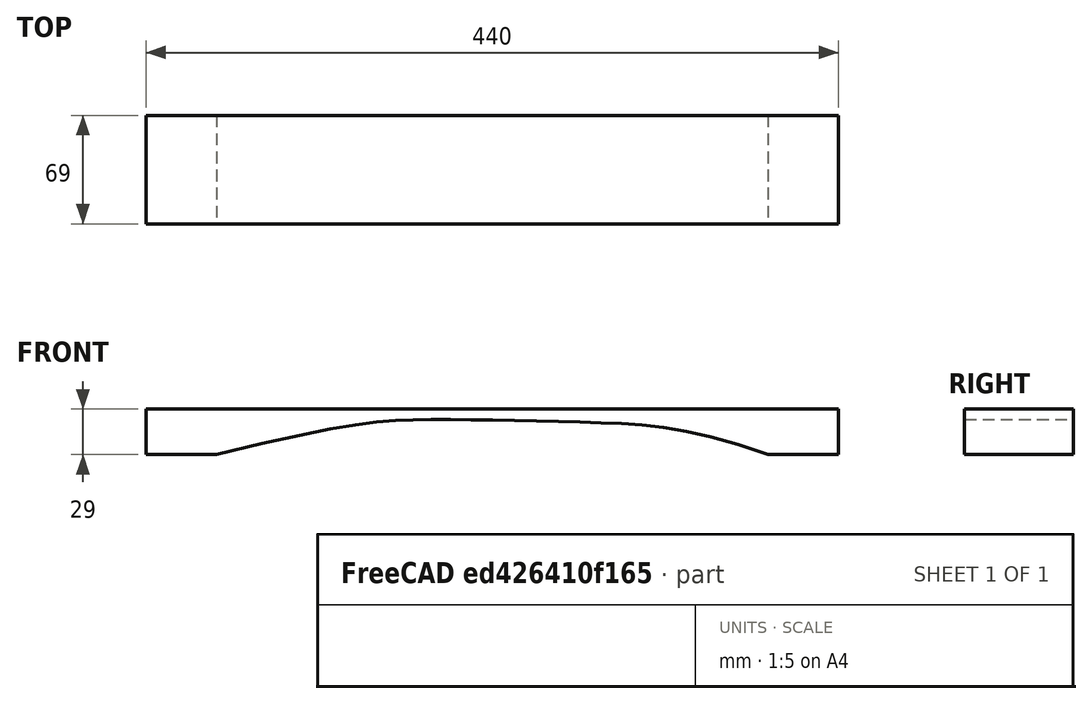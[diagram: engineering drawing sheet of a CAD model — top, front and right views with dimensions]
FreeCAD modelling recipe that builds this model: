
FCSTD DOCUMENT  (FreeCAD 0.20R29410 (Git))
Label: EuropeanOak-6.67-Bar
License: All rights reserved
LicenseURL: http://en.wikipedia.org/wiki/All_rights_reserved
objects: Fem::FemResultObjectPython×3, Fem::FemPostDataAtPointFilter×3, Fem::FemPostWarpVectorFilter×3, Fem::FemPostPipeline×3, Sketcher::SketchObject×1, Part::Extrusion×1, Fem::FemSolverObjectPython×1, App::MaterialObjectPython×1, Fem::ConstraintDisplacement×1, Fem::FemMeshShapeNetgenObject×1, Fem::FemMeshObjectPython×1, App::TextDocument×1, Fem::FemAnalysis×1
note: 2 computed .brp shape members not serialized (recipe doc carries the construction recipe); baked Part::Feature solids carry a one-line shape summary decoded from their .brp

FEATURE [Sketcher::SketchObject] Sketch
  FullyConstrained = true
  Placement = pos=(0,0,0) rot=(1,0,0;1.5708rad)
  sketch-geometry (12):
    g0: LineSegment StartX=44.78 StartY=0 StartZ=0 EndX=0 EndY=0 EndZ=0
    g1: LineSegment StartX=0 StartY=0 StartZ=0 EndX=0 EndY=29 EndZ=0
    g2: LineSegment StartX=0 StartY=29 StartZ=0 EndX=440 EndY=29 EndZ=0
    g3: LineSegment StartX=440 StartY=29 StartZ=0 EndX=440 EndY=0 EndZ=0
    g4: LineSegment StartX=440 StartY=0 StartZ=0 EndX=395.22 EndY=0 EndZ=0
    g5-g10: Circle x6 (B-spline internal-alignment scaffolding for g11; pole/knot coordinates omitted)
    g11: BSplineCurve PolesCount=6 KnotsCount=4 Degree=3 IsPeriodic=0
  constraints (38):
    c: DistanceX(g0) = 0
    c: DistanceY(g0) = 0
    c: Distance(g1,g1) = 29
    c: Distance(g2,g2) = 440
    c: DistanceX(g0,g0) = 44.78
    c: DistanceX(g4,g4) = 44.78
    c: Horizontal(g0)
    c: Vertical(g1)
    c: Horizontal(g2)
    c: Vertical(g3)
    c: Horizontal(g4)
    c: Equal(g3,g1)
    c: Coincident(g0,g1)
    c: Coincident(g1,g2)
    c: Coincident(g2,g3)
    c: Coincident(g3,g4)
    c: DistanceX(g6) = 343.71
    c: DistanceY(g6) = 18.63
    c: DistanceX(g7) = 284.82
    c: DistanceY(g7) = 20.42
    c: DistanceX(g8) = 168.2
    c: DistanceY(g8) = 23.47
    c: DistanceX(g9) = 126.8
    c: DistanceY(g9) = 20.13
    c: Weight(g5) = 1
    c: InternalAlignment(g5,g11)
    c: Weight(g6) = 1
    c: InternalAlignment(g6,g11)
    c: Weight(g7) = 1
    c: InternalAlignment(g7,g11)
    c: Weight(g8) = 1
    c: InternalAlignment(g8,g11)
    c: Weight(g9) = 1
    c: InternalAlignment(g9,g11)
    c: Weight(g10) = 1
    c: InternalAlignment(g10,g11)
    c: Coincident(g4,g11)
    c: Coincident(g0,g11)
FEATURE [Part::Extrusion] Bar
  Base = -> Sketch
  Dir = (0,-1,2e-16)
  DirMode = 2
  FaceMakerClass = Part::FaceMakerBullseye
  LengthFwd = 69
  LengthRev = 0
  Solid = true
  Symmetric = false
FEATURE [Fem::FemSolverObjectPython] SolverCcxTools  # FEM object (typed FeaturePython)
  AnalysisType = 1
  BeamShellResultOutput3D = false
  BucklingFactors = 1
  EigenmodeHighLimit = 20000
  EigenmodeLowLimit = 100
  EigenmodesCount = 6
  GeometricalNonlinearity = 0
  IterationsControlParameterCutb = 0.25,0.5,0.75,0.85,,,1.5,
  IterationsControlParameterIter = 4,8,9,200,10,400,,200,,
  IterationsControlParameterTimeUse = false
  IterationsThermoMechMaximum = 2000
  IterationsUserDefinedIncrementations = false
  IterationsUserDefinedTimeStepLength = false
  MaterialNonlinearity = 0
  MatrixSolverType = 0
  SplitInputWriter = false
  ThermoMechSteadyState = false
  TimeEnd = 1
  TimeInitialStep = 0.01
FEATURE [App::MaterialObjectPython] MaterialSolid  # material (typed FeaturePython)
  Category = 0
  Material = CompressiveStrength=7800 kPa,Density=670 kg/m^3,Name=White European Oak,PoissonRatio=0.37,ShearModulus=11.6 MPa,UltimateTensileStrength=97.1 MPa,+1 more (map truncated)
FEATURE [Fem::ConstraintDisplacement] FemConstraintDisplacement
  NormalDirection = (0,-2e-16,-1)
  Normals = (116) [(0,-2.2e-16,-1),(0,-2.2e-16,-1),(0,-2.2e-16,-1),(0,-2.2e-16,-1),(0,-2.2e-16,-1),(0,-2.2e-16,-1),(0,-2.2e-16,-1),(0,-2.2e-16,-1),(0,-2.2e-16,-1),+107 more]
  Points = (116) [(44.78,-69,1.518e-14),(29.8533,-69,1.518e-14),(14.9267,-69,1.518e-14),(0,-69,1.518e-14),(44.78,-46,1.012e-14),(29.8533,-46,1.012e-14),+110 more]
  References = -> [Bar]
  rotxFix = false
  rotxFree = true
  rotyFix = false
  rotyFree = true
  rotzFix = false
  rotzFree = true
  xDisplacement = 0
  xFix = false
  xFree = true
  xRotation = 0
  yDisplacement = 0
  yFix = true
  yFree = false
  yRotation = 0
  zDisplacement = 0
  zFix = false
  zFree = true
  zRotation = 0
FEATURE [Fem::FemMeshShapeNetgenObject] FEMMeshNetgen
  Fineness = 4
  GrowthRate = 0.3
  MaxSize = 10
  NbSegsPerEdge = 1
  NbSegsPerRadius = 2
  Optimize = true
  SecondOrder = true
  Shape = -> Bar
FEATURE [Fem::FemMeshObjectPython] ResultMesh  # FEM object (typed FeaturePython)
FEATURE [Fem::FemResultObjectPython] CCX_EigenMode_4_Results  # FEM object (typed FeaturePython)
  DisplacementLengths = [39.76,39.7598,79.6677,79.6678,75.5133,75.5134,78.2101,78.2101,82.2686,82.2687,40.3463,40.3463,49.9702,60.3738,71.2113,79.6902,78.2819,67.6655,57.1744,46.6504,36.1976,25.8005,15.5235,6.29701,7.66099,17.2706,27.454,37.6931,47.9022,57.8919,+6003 more]
  DisplacementVectors = (6033) [(-25.6275,0,-30.3988),(-25.6276,0,-30.3985),(-25.6346,0,-75.4308),(-25.6347,0,-75.4309),(3.52913,0,-75.4308),(3.52922,0,-75.4309),+6027 more]
  Eigenmode = 4
  EigenmodeFrequency = 130.981
  MaxShear = [1.94221,1.98751,0.103232,0.0983929,0.0331848,0.0304907,0.0614545,0.0502109,0.0808435,0.106342,2.57597,2.6428,1.8565,0.930537,0.220849,0.0864277,0.0953536,0.131411,0.619313,1.415,2.5679,4.35116,6.86131,10.7409,16.0052,23.8974,34.7322,+6006 more]
  Mesh = -> ResultMesh
  NodeNumbers = [1,2,3,4,5,6,7,8,9,10,11,12,13,14,15,16,17,18,19,20,21,22,23,24,25,26,27,28,29,30,31,32,33,34,35,36,37,38,39,40,41,42,43,44,45,46,47,48,49,50,51,52,53,54,55,56,57,58,59,60,61,62,63,64,65,66,67,68,69,+5964 more]
  NodeStrainXX = [-0.000295432,-0.00030086,2.45907e-06,6.97468e-07,-5.1885e-07,-3.24382e-07,-4.21691e-06,-9.08742e-07,4.74133e-06,9.43238e-08,-0.000403341,-0.000414238,-0.000302757,-0.000149992,-3.57943e-05,-8.17154e-06,6.68297e-06,2.06383e-05,0.000100366,+6014 more]
  NodeStrainXY = [1.45659e-07,-1.30851e-06,7.3266e-08,-3.18589e-07,1.00641e-06,-1.16253e-06,-1.18173e-07,1.44421e-06,3.08405e-07,-2.86151e-07,-4.66795e-06,6.44721e-07,2.1901e-07,9.09316e-07,-9.04872e-07,-8.87817e-07,5.29394e-07,6.16621e-07,4.68293e-07,+6014 more]
  NodeStrainXZ = [9.55077e-05,9.82858e-05,1.3336e-05,1.26362e-05,4.07302e-06,3.65005e-06,-7.61538e-06,-6.238e-06,-1.00674e-05,-1.36201e-05,-8.9149e-05,-8.78961e-05,9.79878e-06,1.08867e-05,2.8033e-06,4.45075e-06,8.31595e-06,3.36125e-06,3.86984e-06,+6014 more]
  NodeStrainYY = [-2.86839e-11,-2.76119e-11,-2.19101e-07,-2.12745e-07,0,0,9.10746e-13,0,4.5424e-14,-1.13863e-07,1.03284e-06,-4.94041e-07,-2.90461e-07,-2.61899e-08,3.27789e-13,5.90685e-07,-1.07211e-07,-5.50318e-12,-6.07976e-13,1.50491e-12,1.64431e-12,+6012 more]
  NodeStrainYZ = [-1.68788e-06,6.43692e-07,1.89881e-07,-8.10458e-07,6.91778e-07,-7.41743e-07,1.089e-07,-7.08997e-07,3.35057e-07,-1.96548e-07,-2.12959e-06,-7.26048e-07,7.29178e-07,9.46325e-08,4.64683e-07,3.25619e-07,-3.56037e-07,2.91515e-07,6.07891e-07,+6014 more]
  NodeStrainZZ = [0.000168837,0.000173793,1.74266e-06,3.03079e-06,-1.15479e-06,-1.08002e-06,2.81428e-07,-1.77176e-06,-7.60119e-07,3.70239e-06,0.000238139,0.000245892,0.000176727,8.95502e-05,2.09848e-05,1.222e-05,-1.14644e-05,-1.26343e-05,-5.95246e-05,+6014 more]
  NodeStressXX = [-3.67972,-3.72691,0.0628778,0.0441046,-0.0224424,-0.0179732,-0.0759594,-0.0365453,0.0805206,0.0412805,-4.92836,-5.06409,-3.73338,-1.82631,-0.440011,-0.0121447,-0.00211965,0.247812,1.22625,2.81066,5.10876,8.66193,13.6774,21.4132,31.8491,+6008 more]
  NodeStressXY = [0.001127,-0.0101242,0.000566876,-0.002465,0.00778681,-0.00899475,-0.00091433,0.0111742,0.0023862,-0.00221402,-0.036117,0.00498836,0.00169453,0.00703558,-0.0070012,-0.00686924,0.00409604,0.00477093,0.00362329,0.00546462,0.00611664,0.0117295,+6011 more]
  NodeStressXZ = [0.738965,0.760459,0.103184,0.0977689,0.0315139,0.0282412,-0.0589219,-0.0482648,-0.0778938,-0.105382,-0.689766,-0.680072,0.0758154,0.0842329,0.0216898,0.0344365,0.0643424,0.0260067,0.0299418,0.0372396,0.0480075,0.144833,0.188619,0.359045,+6009 more]
  NodeStressYY = [-1.3939,-1.39909,0.0421562,0.0370621,-0.0184279,-0.0154634,-0.0433322,-0.0295141,0.0438358,0.0396697,-1.79962,-1.86286,-1.39313,-0.665992,-0.163062,0.0556506,-0.0546569,0.0881289,0.449692,1.03316,1.88059,3.1918,5.04584,7.90212,11.7296,+6008 more]
  NodeStressYZ = [-0.0130595,0.00498039,0.00146915,-0.0062707,0.00535244,-0.00573903,0.000842587,-0.00548567,0.00259241,-0.00152073,-0.0164771,-0.0056176,0.00564181,0.000732193,0.00359536,0.00251939,-0.00275474,0.00225552,0.00470339,0.000629211,0.0102274,+6012 more]
  NodeStressZZ = [-0.0875655,-0.0544186,0.0573349,0.0621581,-0.0273628,-0.0238198,-0.0411548,-0.0432226,0.0379546,0.0691969,0.0349169,0.0434882,-0.0235053,0.0270803,-0.000698001,0.145629,-0.14253,-0.00962542,-0.0108639,-0.0183342,-0.0260827,-0.0354289,+6011 more]
  PrincipalMax = [0.0586206,0.0968262,0.163344,0.151662,0.00980705,0.0115957,0.00291323,0.0119308,0.139988,0.161542,0.129061,0.132508,-0.0219331,0.0309022,0.000434787,0.152829,0.0230074,0.250565,1.22699,2.81117,5.10922,8.66437,13.68,21.4192,31.8554,47.6937,+6007 more]
  PrincipalMed = [-1.394,-1.39905,0.0421444,0.0367868,-0.0214776,-0.0194664,-0.0433638,-0.0327217,0.0440225,0.0397472,-1.79924,-1.86287,-1.39315,-0.665952,-0.162942,0.0563315,-0.054614,0.0880079,0.44972,1.03314,1.88063,3.19189,5.04582,7.90242,11.7308,17.607,+6007 more]
  PrincipalMin = [-3.8258,-3.8782,-0.0431199,-0.0451239,-0.0565626,-0.0493857,-0.119996,-0.0884911,-0.0216993,-0.051142,-5.02288,-5.1531,-3.73493,-1.83017,-0.441264,-0.020026,-0.1677,-0.0122576,-0.0116343,-0.0188246,-0.0265857,-0.0379518,-0.0426047,+6010 more]
  ResultType = Fem::ResultMechanical
  Stats = [-25.6347,25.9336,-0.0014929,0.00150639,-78.0742,106.569,0.763143,106.571,0.00875485,578.029,-17.7689,656.814,-245.14,243.457,-660.917,13.3385,0.00500687,330.025,0,0,0,0,0,0,0,0]
  Time = 0
  vonMises = [3.39945,3.4774,0.179704,0.171217,0.0575092,0.0528146,0.107519,0.0871454,0.140839,0.184837,4.50848,4.62302,3.25196,1.62859,0.386816,0.150035,0.166107,0.229732,1.08425,2.47759,4.49654,7.61939,12.0156,18.8097,28.0262,41.8517,60.8254,89.0578,+6005 more]
FEATURE [Fem::FemResultObjectPython] CCX_EigenMode_5_Results  # FEM object (typed FeaturePython)
  DisplacementLengths = [26.3796,26.3798,75.2426,75.2436,72.5186,72.5197,66.9934,66.9937,69.7371,69.7373,24.8668,24.8666,32.4211,43.6382,56.3709,66.5666,65.5722,54.3498,41.963,29.9872,19.4006,13.6524,18.0852,28.1095,39.5246,51.2307,62.6848,73.5978,83.6074,92.0931,+6003 more]
  DisplacementVectors = (6033) [(-25.4039,0,-7.10821),(-25.4048,0,-7.10547),(-25.5047,0,-70.7881),(-25.5057,0,-70.7888),(15.7479,0,-70.7881),(15.7491,0,-70.7889),(13.7643,0,65.5642),+6026 more]
  Eigenmode = 5
  EigenmodeFrequency = 524.853
  MaxShear = [26.7626,27.199,1.48512,1.42254,0.486505,0.449464,0.798575,0.653579,1.03961,1.37504,31.7685,32.4682,23.5642,12.2071,3.07377,1.14814,1.25091,2.14019,8.84753,19.0198,32.825,52.8687,79.4878,117.768,166.133,232.711,316.08,427.182,565.021,+6004 more]
  Mesh = -> ResultMesh
  NodeNumbers = <same value as first occurrence — deduplicated (x3 in doc)>
  NodeStrainXX = [-0.00408177,-0.00412737,3.00783e-05,3.41267e-06,-5.40461e-06,-2.55257e-06,5.30576e-05,9.77597e-06,-5.71406e-05,4.7807e-06,0.00498277,0.00509671,0.00384536,0.00197003,0.000497902,0.000108019,-8.39451e-05,-0.000338979,-0.00143456,-0.00308963,+6013 more]
  NodeStrainXY = [2.79895e-06,-2.10261e-05,1.39684e-06,-4.19528e-06,1.50869e-05,-1.72684e-05,1.41845e-06,-1.90974e-05,-3.66192e-06,3.22767e-06,5.51717e-05,-6.08049e-06,-1.80597e-06,-1.16568e-05,1.16464e-05,1.14972e-05,-7.12222e-06,-7.95565e-06,-5.67877e-06,+6014 more]
  NodeStrainXZ = [0.00129631,0.00132659,0.00019192,0.000182059,5.9471e-05,5.36167e-05,9.95335e-05,8.10169e-05,0.000130455,0.000175322,0.0010785,0.00106303,-0.00011805,-0.000139037,-4.14354e-05,-6.15708e-05,-0.000112463,-4.93491e-05,-5.44258e-05,-6.54727e-05,+6013 more]
  NodeStrainYY = [-3.65881e-10,-3.2824e-10,-2.99822e-06,-3.00817e-06,0,0,-1.29471e-11,0,1.27525e-13,1.60707e-06,-1.21685e-05,6.27541e-06,2.93115e-06,6.31625e-07,-4.22181e-12,-7.76339e-06,1.4982e-06,6.78318e-11,2.77572e-12,-2.31363e-11,-3.02419e-11,+6012 more]
  NodeStrainYZ = [-1.8959e-05,1.21412e-05,2.87607e-06,-1.15611e-05,9.85742e-06,-1.02397e-05,-7.72717e-07,8.76256e-06,-4.30751e-06,2.96132e-06,2.63339e-05,5.65384e-06,-8.68738e-06,-7.19988e-08,-5.88968e-06,-4.34136e-06,4.51115e-06,-3.98521e-06,-5.92133e-06,+6014 more]
  NodeStrainZZ = [0.00233178,0.00238333,2.89764e-05,4.90677e-05,-1.90257e-05,-1.81866e-05,-1.44209e-06,2.50754e-05,5.97215e-06,-5.25978e-05,-0.00293993,-0.00302224,-0.00224114,-0.00117303,-0.000291925,-0.000160745,0.000147755,0.00020511,0.000849787,+6014 more]
  NodeStressXX = [-50.8501,-51.1374,0.849942,0.571126,-0.310811,-0.248102,0.97884,0.459376,-1.00551,-0.471814,60.912,62.3448,47.4482,24.025,6.12031,0.169733,0.069583,-4.09674,-17.5383,-37.829,-65.3777,-105.38,-158.599,-235.073,-331.034,-465.016,-630.942,+6006 more]
  NodeStressXY = [0.0216561,-0.162684,0.0108077,-0.0324598,0.116731,-0.13361,0.0109748,-0.147761,-0.0283331,0.0249732,0.426876,-0.0470461,-0.0139732,-0.0901917,0.0901109,0.0889563,-0.0551062,-0.0615547,-0.043938,-0.0597385,-0.0607592,-0.122721,-0.120457,+6010 more]
  NodeStressXZ = [10.0299,10.2641,1.48493,1.40863,0.460141,0.414845,0.770113,0.626846,1.00936,1.35651,8.34457,8.22494,-0.913376,-1.07576,-0.320595,-0.476387,-0.870151,-0.381825,-0.421105,-0.506577,-0.624193,-1.68192,-2.10195,-3.66855,-4.14152,-8.43431,+6007 more]
  NodeStressYY = [-19.2686,-19.203,0.594021,0.521447,-0.268994,-0.228352,0.568321,0.383737,-0.563399,-0.496369,22.2649,22.9589,17.7184,8.7873,2.26794,-0.726099,0.730677,-1.47398,-6.43879,-13.9239,-24.0935,-38.8787,-58.5627,-86.849,-122.072,-172.025,-233.299,+6006 more]
  NodeStressYZ = [-0.14669,0.093939,0.0222528,-0.0894512,0.0762691,-0.0792269,-0.00597869,0.0677979,-0.0333281,0.0229124,0.203751,0.043745,-0.0672163,-0.000557071,-0.0455698,-0.0335901,0.0349038,-0.0308345,-0.0458146,-0.00545148,-0.0892403,-0.207058,+6011 more]
  NodeStressZZ = [-1.22703,-0.762681,0.841416,0.92437,-0.416201,-0.369066,0.557163,0.577752,-0.517191,-0.915765,-0.387802,-0.473381,0.355546,-0.29361,0.00924369,-1.90975,1.8623,0.112998,0.136212,0.19701,0.260087,0.302503,0.320904,0.345852,1.10896,0.0845051,+6007 more]
  PrincipalMax = [0.724535,1.24858,2.33093,2.17216,0.145551,0.169519,1.56648,1.15145,0.279387,0.681736,62.0327,63.4039,47.4659,24.073,6.13929,0.282448,2.21708,0.147741,0.146544,0.203759,0.266345,0.330336,0.348701,0.405826,1.17582,0.239062,0.807719,7.51071,+6005 more]
  PrincipalMed = [-19.2695,-19.2023,0.59376,0.517715,-0.3141,-0.28563,0.568512,0.425131,-0.565664,-0.497342,22.2607,22.959,17.7187,8.78677,2.26647,-0.734725,0.730202,-1.47283,-6.43891,-13.9238,-24.0937,-38.8795,-58.5626,-86.8516,-122.082,-172.012,-233.292,+6006 more]
  PrincipalMin = [-52.8008,-53.1494,-0.639311,-0.672931,-0.827458,-0.729409,-0.0306687,-0.155712,-1.79982,-2.06834,-1.50431,-1.53254,0.337576,-0.341107,-0.00826089,-2.01384,-0.284727,-4.13264,-17.5485,-37.8359,-65.3837,-105.407,-158.627,-235.13,-331.091,+6008 more]
  ResultType = Fem::ResultMechanical
  Stats = [-25.506,15.7494,-0.00761638,0.00848591,-101.15,101.352,0.502546,101.646,0.439248,2127.44,-75.6159,2443.28,-895.398,916.808,-2414.85,86.8957,0.251429,1214.72,0,0,0,0,0,0,0,0]
  Time = 0
  vonMises = [46.8458,47.5909,2.58462,2.47481,0.843078,0.778515,1.39747,1.13437,1.81113,2.38969,55.6037,56.7995,41.28,21.3663,5.38356,1.99295,2.17944,3.74316,15.4904,33.3046,57.4813,92.5843,139.206,206.25,290.928,407.577,553.57,747.905,990.249,1249.3,+6003 more]
FEATURE [Fem::FemResultObjectPython] CCX_EigenMode_6_Results  # FEM object (typed FeaturePython)
  DisplacementLengths = [27.832,27.838,66.7128,66.7173,62.6082,62.6128,55.4381,55.4396,58.4251,58.4262,22.3434,22.3428,25.5019,34.436,45.9283,54.9139,53.8183,43.4024,31.746,20.9804,13.5653,15.0889,23.5549,33.6012,43.5138,52.5274,59.9044,64.8659,66.3161,62.9167,+6003 more]
  DisplacementVectors = (6033) [(-27.208,0,5.86049),(-27.2115,0,5.87246),(-27.7362,0,-60.6737),(-27.7404,0,-60.6768),(15.4442,0,-60.6734),(15.4497,0,-60.6768),(-13.3287,0,-53.812),+6026 more]
  Eigenmode = 6
  EigenmodeFrequency = 1303.91
  MaxShear = [136.037,137.464,7.61522,7.32084,2.52786,2.34463,3.96261,3.24666,5.12904,6.80576,154.552,157.581,116.944,62.0681,16.4273,5.76864,6.24324,11.3255,45.0952,94.5012,159.068,249.183,364.022,520.072,705.085,939.152,1203.39,1508.33,1825.93,2074.04,+6003 more]
  Mesh = -> ResultMesh
  NodeNumbers = <same value as first occurrence — deduplicated (x3 in doc)>
  NodeStrainXX = [-0.020788,-0.0208971,0.000134744,-6.90894e-06,-2.0077e-05,-5.3893e-06,-0.000258191,-4.26769e-05,0.000270665,-4.09486e-05,-0.024265,-0.0247574,-0.0190922,-0.0100261,-0.00266122,-0.000541081,0.000408383,0.00179632,0.00731274,0.0153548,+6013 more]
  NodeStrainXY = [1.73553e-05,-0.000117298,8.32893e-06,-2.01082e-05,7.95352e-05,-9.05067e-05,-6.70066e-06,9.5688e-05,1.71716e-05,-1.45595e-05,-0.00026063,2.39464e-05,5.84878e-06,5.73628e-05,-5.74711e-05,-5.69508e-05,3.60348e-05,3.93199e-05,2.7026e-05,+6014 more]
  NodeStrainXZ = [0.00651596,0.00663732,0.000983996,0.000933997,0.000307925,0.000278744,-0.000495457,-0.000401824,-0.000646242,-0.000865102,-0.00518863,-0.00511502,0.000554954,0.000683235,0.000220146,0.000316316,0.0005705,0.000261116,0.000281667,0.000332063,+6013 more]
  NodeStrainYY = [-1.73928e-09,-1.4383e-09,-1.48113e-05,-1.52243e-05,0,0,6.73896e-11,0,-2.78901e-12,-8.33989e-06,5.7675e-05,-3.10318e-05,-1.16882e-05,-3.94659e-06,2.06505e-11,3.87545e-05,-7.73077e-06,-3.26021e-10,8.34234e-13,1.2487e-10,1.75449e-10,+6012 more]
  NodeStrainYZ = [-8.09555e-05,7.27873e-05,1.51979e-05,-5.89262e-05,5.01335e-05,-5.08979e-05,2.0046e-06,-4.21819e-05,2.12362e-05,-1.58963e-05,-0.000128514,-1.64559e-05,4.19252e-05,-3.03465e-06,2.87636e-05,2.18677e-05,-2.20545e-05,2.03801e-05,2.37808e-05,+6014 more]
  NodeStrainZZ = [0.0118717,0.0120623,0.000162852,0.000271601,-0.000106278,-0.000102845,7.36528e-07,-0.000130256,-1.84337e-05,0.000273865,0.0143102,0.0146702,0.0111162,0.00595926,0.00156047,0.000802965,-0.000729842,-0.00108306,-0.00433011,-0.00906385,+6013 more]
  NodeStressXX = [-259.016,-258.963,4.1562,2.69335,-1.5466,-1.23343,-4.83242,-2.23431,4.87142,2.15591,-296.718,-302.962,-235.669,-122.397,-32.7104,-0.876241,-0.464855,21.752,89.4211,188.07,317.005,497.05,726.748,1038.97,1406.29,1879.08,2404.86,2991.1,+6005 more]
  NodeStressXY = [0.134282,-0.907561,0.0644428,-0.155582,0.615382,-0.700271,-0.0518445,0.74036,0.13286,-0.11265,-2.01656,0.185279,0.0452533,0.443829,-0.444667,-0.440641,0.27881,0.304227,0.209106,0.264521,0.24937,0.527898,0.443015,0.622601,-3.69359,7.40389,+6007 more]
  NodeStressXZ = [50.4155,51.3544,7.6134,7.22654,2.38248,2.1567,-3.83347,-3.109,-5.00012,-6.69349,-40.1456,-39.576,4.29381,5.28634,1.70332,2.44741,4.41409,2.02031,2.17932,2.56925,3.0872,7.78775,9.46385,15.4515,16.9243,31.9266,53.865,155.611,140.324,207.625,+6003 more]
  NodeStressYY = [-98.1743,-97.2772,2.99905,2.62901,-1.39125,-1.19173,-2.83474,-1.90411,2.77723,2.40821,-108.528,-111.648,-88.0394,-44.853,-12.12,3.61008,-3.68442,7.85344,32.8408,69.2671,116.896,183.514,268.508,384.158,519.065,695.968,889.989,1103.22,+6005 more]
  NodeStressYZ = [-0.626371,0.563172,0.11759,-0.455925,0.387894,-0.393808,0.01551,-0.326371,0.164309,-0.122993,-0.994342,-0.127323,0.324385,-0.0234798,0.22255,0.169195,-0.170641,0.157685,0.183998,0.0187531,0.322847,0.912303,-0.145957,1.98102,-5.19222,+6008 more]
  NodeStressZZ = [-6.3199,-3.94843,4.37367,4.84824,-2.21355,-1.98746,-2.82904,-2.91192,2.6346,4.5917,1.74778,2.09882,-1.94016,1.28565,-0.0462303,9.52295,-9.27156,-0.526475,-0.662243,-0.861917,-1.07087,-1.06679,-1.05002,-0.705016,-3.40794,1.91512,0.513105,+6006 more]
  PrincipalMax = [3.37059,6.00616,11.881,11.1008,0.765518,0.880426,0.132102,0.775798,8.87668,10.1773,7.05782,7.14964,-1.86008,1.51118,0.0456135,10.0709,1.37398,21.9409,89.4746,188.106,317.035,497.173,726.871,1039.2,1406.51,1879.67,2406.09,2999.17,3698.41,+6004 more]
  PrincipalMed = [-98.1774,-97.2728,2.99739,2.61068,-1.62671,-1.48422,-2.83519,-2.10862,2.78797,2.41282,-108.509,-111.648,-88.0406,-44.8505,-12.1132,3.65229,-3.68231,7.84827,32.8409,69.2665,116.897,183.517,268.508,384.167,519.1,695.928,889.97,1103.2,1385.12,+6004 more]
  PrincipalMin = [-268.703,-268.922,-3.34945,-3.54088,-4.29021,-3.80882,-7.79311,-5.71751,-1.3814,-3.43426,-302.047,-308.013,-235.748,-122.625,-32.809,-1.46639,-11.1125,-0.710171,-0.715889,-0.896853,-1.1017,-1.19294,-1.17315,-0.944697,-3.66179,1.36592,+6007 more]
  ResultType = Fem::ResultMechanical
  Stats = [-27.7418,22.754,-0.0172899,0.014936,-158.053,76.3135,0.145871,158.054,2.59078,4857.09,-241.243,5462.3,-2082.44,2023.27,-5552.43,252.559,1.4946,2773.22,0,0,0,0,0,0,0,0]
  Time = 0
  vonMises = [238.134,240.536,13.2508,12.7339,4.38049,4.06106,6.93523,5.63503,8.93545,11.8268,270.517,275.68,204.876,108.646,28.7713,10.0127,10.8786,19.8106,78.9549,165.48,278.559,436.386,637.524,910.846,1234.78,1644.94,2107.67,2641.1,3199.93,3632.33,+6003 more]
FEATURE [App::TextDocument] ccx_dat_file
  Text = <blob: 2957 chars omitted>
FEATURE [Fem::FemPostDataAtPointFilter] DataAtPoint
  Center = (365,-35,25.48)
  FieldName = Displacement
  PointData = [6.40636e-05,6.40636e-05,6.40636e-05,6.40636e-05,6.40636e-05,6.40636e-05,6.40636e-05,6.40636e-05,6.40636e-05,6.40636e-05]
  Radius = 0
  Unit = m
FEATURE [Fem::FemPostWarpVectorFilter] WarpVector
  Factor = 0
  Vector = 0
FEATURE [Fem::FemPostPipeline] ResultPipeline
  Filter = -> [DataAtPoint,WarpVector]
  Mode = 2
FEATURE [Fem::FemPostWarpVectorFilter] WarpVector001
  Factor = 0
  Vector = 0
FEATURE [Fem::FemPostDataAtPointFilter] DataAtPoint001
  Center = (390,-69,18.45)
  FieldName = Displacement
  PointData = [0.000784629,0.000784629,0.000784629,0.000784629,0.000784629,0.000784629,0.000784629,0.000784629,0.000784629,0.000784629]
  Radius = 0
  Unit = m
FEATURE [Fem::FemPostPipeline] ResultPipeline001
  Filter = -> [WarpVector001,DataAtPoint001]
  Mode = 2
FEATURE [Fem::FemPostWarpVectorFilter] WarpVector002
  Factor = 0
  Vector = 0
FEATURE [Fem::FemPostDataAtPointFilter] DataAtPoint002
  Center = (399,-39,18.61)
  FieldName = Intermediate Principal Stress
  Input = -> WarpVector002
  PointData = [30842600,30842600,30842600,30842600,30842600,30842600,30842600,30842600,30842600,30842600]
  Radius = 0
  Unit = Pa
FEATURE [Fem::FemPostPipeline] ResultPipeline002
  Filter = -> [WarpVector002,DataAtPoint002]
  Mode = 2
FEATURE [Fem::FemAnalysis] Analysis
  Group = -> [SolverCcxTools,MaterialSolid,FemConstraintDisplacement,FEMMeshNetgen,CCX_EigenMode_4_Results,CCX_EigenMode_5_Results,CCX_EigenMode_6_Results,ccx_dat_file,ResultPipeline,ResultPipeline001,ResultPipeline002]
